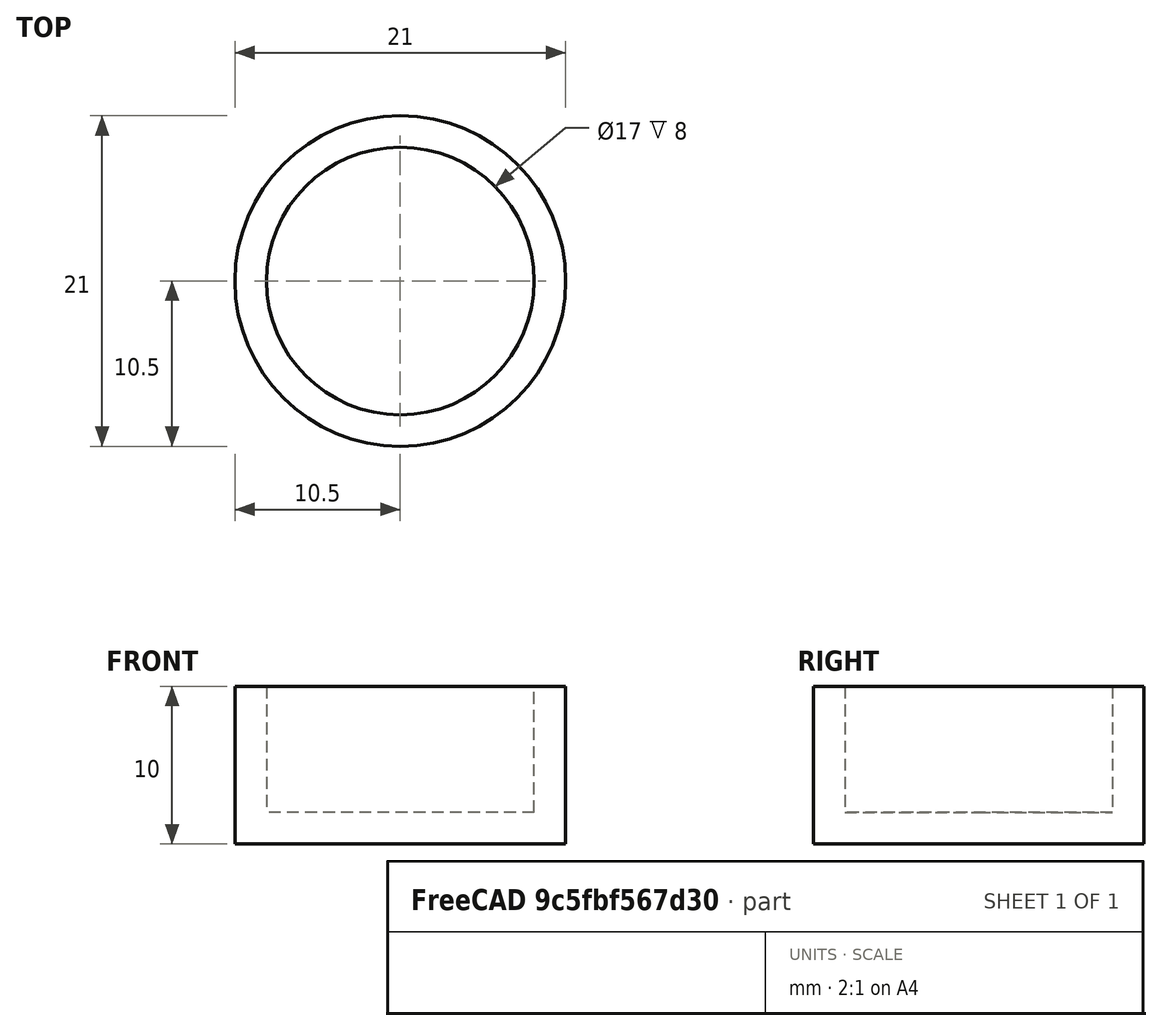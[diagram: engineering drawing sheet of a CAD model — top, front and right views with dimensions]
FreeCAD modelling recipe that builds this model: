
FCSTD DOCUMENT  (FreeCAD 0.21R33771 (Git))
Label: threadedCap
License: All rights reserved
LicenseURL: http://en.wikipedia.org/wiki/All_rights_reserved
objects: Spreadsheet::Sheet×1, PartDesign::AdditiveCylinder×1, PartDesign::SubtractiveCylinder×1, PartDesign::Body×1
note: 5 computed .brp shape members not serialized (recipe doc carries the construction recipe); baked Part::Feature solids carry a one-line shape summary decoded from their .brp

FEATURE [Spreadsheet::Sheet] Spreadsheet  label="measurement"
  cells = A2='outer_dia; B2(outer_dia)==17 mm; A3='thread_step; B3(thread_step)==1 mm; A4='length; B4(length)==8 mm; A5='tolerance; B5(tolerance)==0.4 mm; A6='wall_thickness; B6(wall_thickness)==2 mm
FEATURE [PartDesign::AdditiveCylinder] Cylinder
  Angle = 360
  AttacherType = Attacher::AttachEngine3D
  FirstAngle = 0
  Height = 10
  MapMode = 5
  Radius = 10.5
  SecondAngle = 0
  Support = -> [XY_Plane]
  expr: Height = <<measurement>>.length + <<measurement>>.wall_thickness
  expr: Radius = <<measurement>>.outer_dia / 2 + <<measurement>>.wall_thickness
FEATURE [PartDesign::SubtractiveCylinder] Cylinder001
  Angle = 360
  AttacherType = Attacher::AttachEngine3D
  AttachmentOffset = pos=(0,0,2) rot=(0,0,1;0rad)
  BaseFeature = -> Cylinder
  FirstAngle = 0
  Height = 8
  MapMode = 5
  Placement = pos=(0,0,2) rot=(0,0,1;0rad)
  Radius = 8.5
  SecondAngle = 0
  Support = -> [XY_Plane]
  expr: .AttachmentOffset.Base.z = <<measurement>>.wall_thickness
  expr: Height = <<measurement>>.length
  expr: Radius = Spreadsheet.outer_dia / 2
FEATURE [PartDesign::Body] Body
  Group = -> [Cylinder,Cylinder001]
  Origin = -> Origin
  Tip = -> Cylinder001
